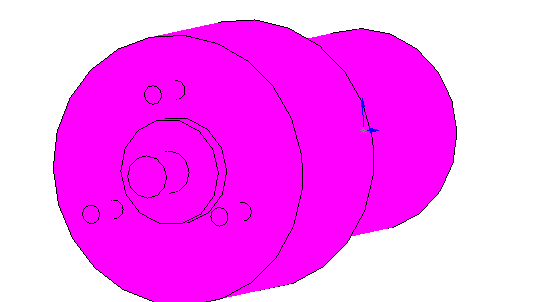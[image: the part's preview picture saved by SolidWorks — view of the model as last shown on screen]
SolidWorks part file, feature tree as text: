
SOLIDWORKS PART (.sldprt)
format: sldprt  version: not decoded by parser v0  size: 140,800 bytes
history: native  units: mm
features: sketch x6, extrude x6 (+11 scaffold rows collapsed)
feature tree (23):
  scaffold x11  (default folders/planes/origin — collapsed)
  sketch  "Sketch1"  dims[D1=30.48mm]
  extrude  "Extrude1"  Depth=43.18mm
  sketch  "Sketch2"  dims[D1=40.64mm]
  extrude  "Extrude2"  Depth=26.924mm
  sketch  "Sketch3"  dims[D1=6.35mm]
  extrude  "Extrude3"  Depth=11.684mm
  sketch  "Sketch4"  dims[D1=15.9004mm]
  extrude  "Extrude4"  Depth=3.175mm
  sketch  "Sketch5"  dims[D1=1.524mm]
  extrude  "Extrude5"  Depth=8.89mm
  sketch  "Sketch6"  dims[D1=24.13mm D2=2.794mm]
  extrude  "Extrude6"  Depth=8.89mm
decode coverage: 12 of 12 modeling features carry decoded parameters
note: suppression state not decoded; provenance and decode notes live in map.json
